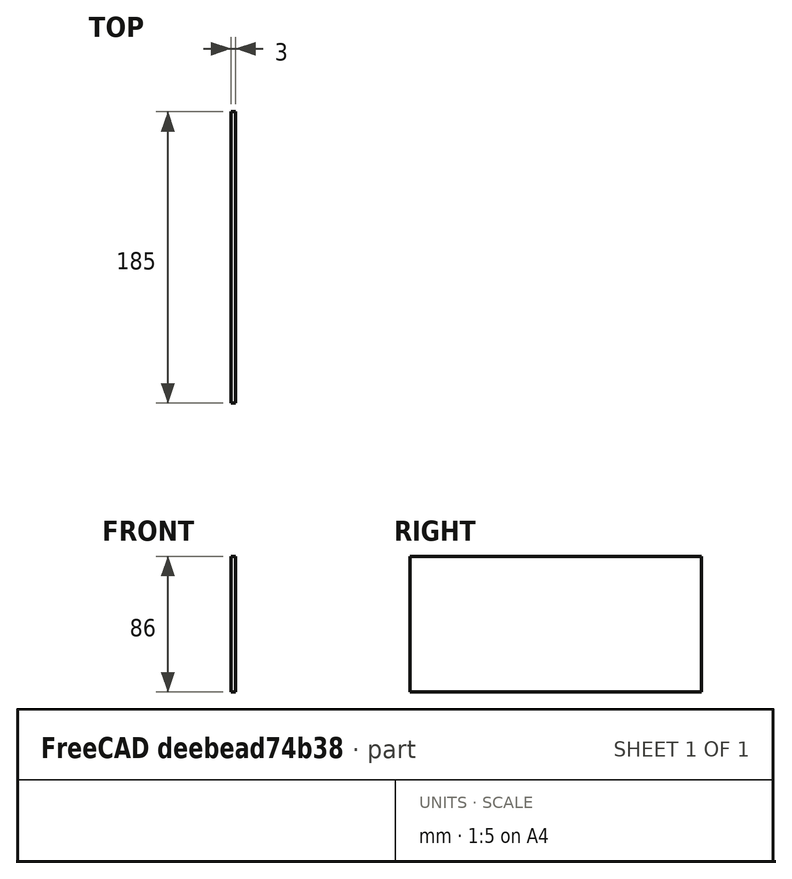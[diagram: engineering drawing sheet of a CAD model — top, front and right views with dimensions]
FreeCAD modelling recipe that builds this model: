
FCSTD DOCUMENT  (FreeCAD 0.20R29410 (Git))
Label: case-bottom-panel
License: All rights reserved
LicenseURL: http://en.wikipedia.org/wiki/All_rights_reserved
objects: Sketcher::SketchObject×1, PartDesign::Pad×1, PartDesign::Body×1
note: 4 computed .brp shape members not serialized (recipe doc carries the construction recipe); baked Part::Feature solids carry a one-line shape summary decoded from their .brp

FEATURE [Sketcher::SketchObject] Sketch  label="skBase"
  FullyConstrained = true
  MapMode = 5
  Placement = pos=(0,0,0) rot=(0.57735,0.57735,0.57735;2.0944rad)
  Support = -> [YZ_Plane]
  sketch-geometry (4):
    g0: LineSegment StartX=-92.5 StartY=43 StartZ=0 EndX=92.5 EndY=43 EndZ=0
    g1: LineSegment StartX=92.5 StartY=43 StartZ=0 EndX=92.5 EndY=-43 EndZ=0
    g2: LineSegment StartX=92.5 StartY=-43 StartZ=0 EndX=-92.5 EndY=-43 EndZ=0
    g3: LineSegment StartX=-92.5 StartY=-43 StartZ=0 EndX=-92.5 EndY=43 EndZ=0
  constraints (10):
    c: Coincident(g0,g1)
    c: Coincident(g2,g3)
    c: Coincident(g3,g0)
    c: Horizontal(g2)
    c: Vertical(g3)
    c: Distance(g1) = 86
    c: Coincident(g2,g1)
    c: Symmetric(g0,g0,g-2)
    c: Distance(g0) = 185
    c: Symmetric(g0,g1,g-1)
FEATURE [PartDesign::Pad] Pad  label="pdBase"
  Direction = (1,-2e-16,3e-16)
  Length = 3
  Length2 = 10
  Placement = pos=(0,0,0) rot=(0.57735,0.57735,0.57735;2.0944rad)
  Profile = -> Sketch
  ReferenceAxis = -> Sketch [N_Axis]
  Type = 0
FEATURE [PartDesign::Body] Body
  Group = -> [Sketch,Pad]
  Origin = -> Origin
  Tip = -> Pad
